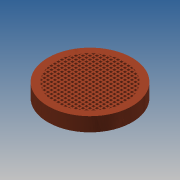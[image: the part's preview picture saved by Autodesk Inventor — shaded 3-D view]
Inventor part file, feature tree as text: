
AUTODESK INVENTOR PART (.ipt)
format: ipt  version: 2014 SP1 (Build 180222100, 222)  size: 1,741,824 bytes
history: native  units: in
note: dims shown in document units (in); Inventor stores cm internally (conversion verified against a paired STEP export)
features: sketch x2, extrude x1, other x1
ambient origin geometry x8: Origin, YZ Plane, XZ Plane, XY Plane, X Axis, Y Axis, Z Axis, Center Point
bodies: Solid1 (feature_tree)
feature tree (4):
  extrude  "Extrusion1"  Depth=1.0in TaperAngle=0.0deg
  other  "Grill4"
  sketch  "Sketch1"  dims[d0=6.0in d1=1.0in d2=0.0in]
  sketch  "Sketch5"  dims[d78=0.5in d79=8.2677in d81=0.25in d82=8.2677in d84=0.25in d87=8.2677in d89=0.25in d90=8.2677in d92=0.25in d95=0.1in d96=1.0in d97=0.0in d98=0.1in d99=1.0in d100=0.0in d101=0.1in d102=0.0in d103=0.0in d104=0.05in d105=0.0in d106=0.0in d107=0.0in d108=18.0529in]
